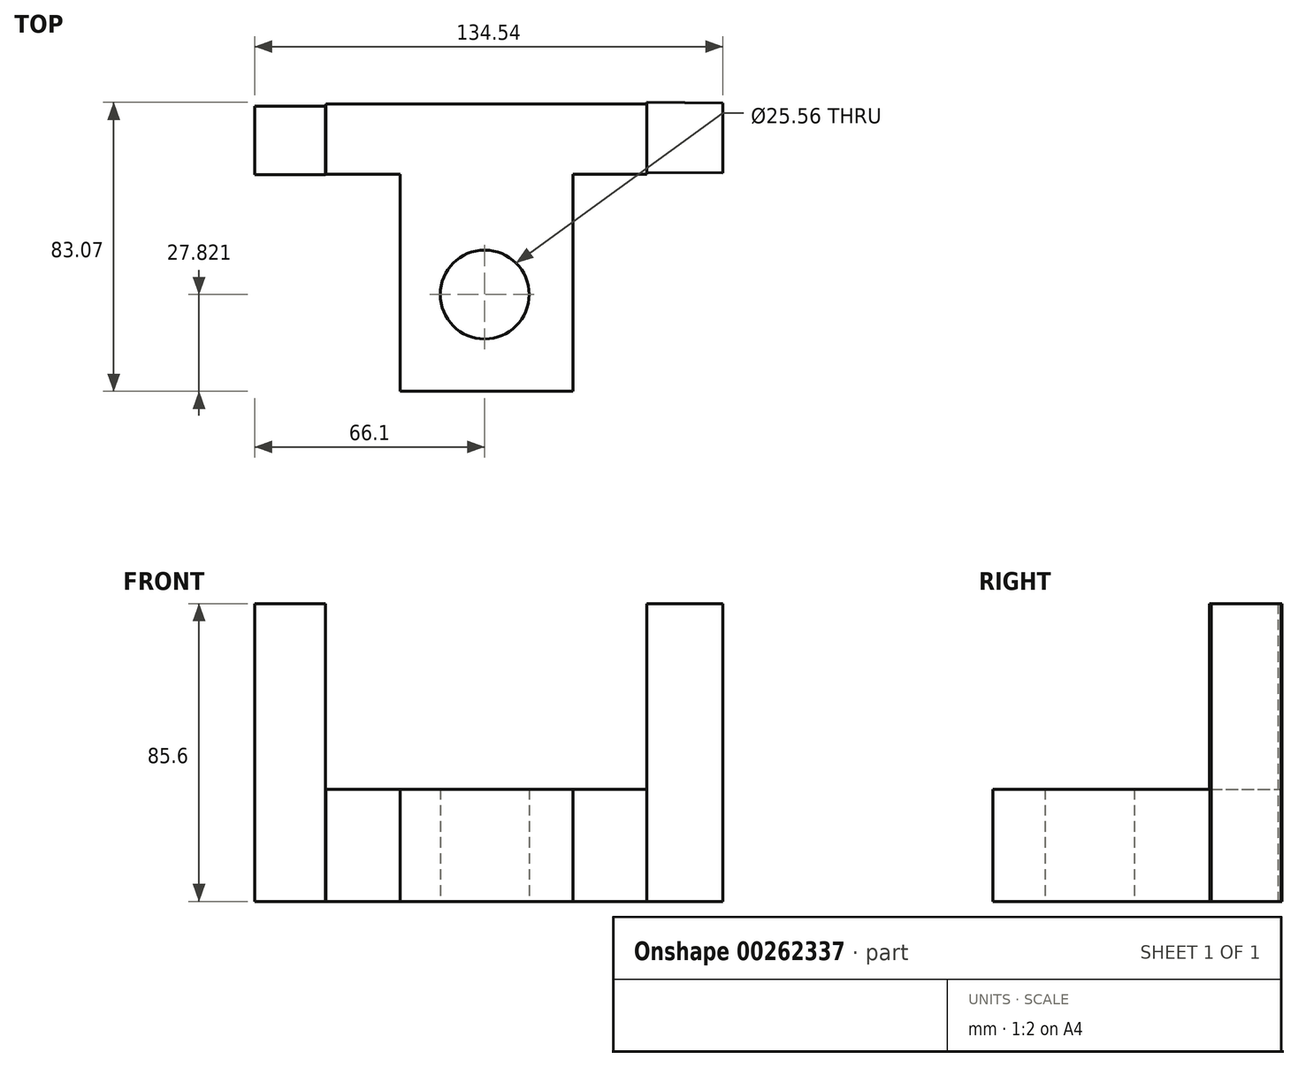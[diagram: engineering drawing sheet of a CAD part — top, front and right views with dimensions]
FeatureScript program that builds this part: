
annotation { "Feature Type Name" : "Feature", "Feature Type Description" : "" }
export const myFeature = defineFeature(function(context is Context, id is Id, definition is map)
    precondition{}
    {
        {
            var Q0;
            Q0=qCreatedBy(makeId("Top.planeOp"),FACE);
            var sketch = newSketch(context, id + "F0", { "sketchPlane" : qUnion([Q0])});
            skLineSegment(sketch, "E0.top", {"start": v(-24.33, -38.9) * mm, "end": v(25.36, -38.9) * mm});
            skLineSegment(sketch, "E0.left", {"start": v(-24.33, 23.47) * mm, "end": v(-24.33, -38.9) * mm});
            skLineSegment(sketch, "E0.right", {"start": v(25.36, 23.47) * mm, "end": v(25.36, -38.9) * mm});
            skLineSegment(sketch, "E1", {"start": v(-24.33, 23.47) * mm, "end": v(-45.57, 23.47) * mm});
            skLineSegment(sketch, "E2", {"start": v(25.36, 23.47) * mm, "end": v(46.6, 23.47) * mm});
            skLineSegment(sketch, "E3", {"start": v(-45.57, 23.47) * mm, "end": v(-45.57, 43.7) * mm});
            skLineSegment(sketch, "E4", {"start": v(-45.57, 43.7) * mm, "end": v(46.6, 43.7) * mm});
            skLineSegment(sketch, "E5", {"start": v(46.6, 43.7) * mm, "end": v(46.6, 23.47) * mm});
            skSolve(sketch);
        }
        {
            var Q0;
            Q0 = qSketchRegion(id + "F0", true);
            extrude(context, id + "F1", {"entities" : qUnion([Q0]), "depth" : 32.26 * mm});
        }
        {
            var Q0;
            Q0=qCreatedBy(makeId("Top.planeOp"),FACE);
            var sketch = newSketch(context, id + "F2", { "sketchPlane" : qUnion([Q0])});
            skLineSegment(sketch, "E6.bottom", {"start": v(-45.81, 43.03) * mm, "end": v(-66.1, 43.03) * mm});
            skLineSegment(sketch, "E6.top", {"start": v(-45.81, 23.4) * mm, "end": v(-66.1, 23.4) * mm});
            skLineSegment(sketch, "E6.left", {"start": v(-45.81, 43.03) * mm, "end": v(-45.81, 23.4) * mm});
            skLineSegment(sketch, "E6.right", {"start": v(-66.1, 43.03) * mm, "end": v(-66.1, 23.4) * mm});
            skLineSegment(sketch, "E7", {"start": v(46.56, 44.18) * mm, "end": v(46.56, 24.02) * mm});
            skLineSegment(sketch, "E8", {"start": v(46.56, 24.02) * mm, "end": v(68.38, 23.84) * mm});
            skLineSegment(sketch, "E9", {"start": v(68.38, 23.84) * mm, "end": v(68.44, 43.97) * mm});
            skLineSegment(sketch, "E10", {"start": v(46.56, 44.18) * mm, "end": v(68.44, 43.97) * mm});
            skSolve(sketch);
        }
        {
            var Q0;
            Q0 = qSketchRegion(id + "F2", true);
            extrude(context, id + "F3", {"entities" : qUnion([Q0]), "operationType" : NewBodyOperationType.ADD, "depth" : 85.6 * mm});
        }
        {
            var Q0;
            Q0=qCreatedBy(makeId("Top.planeOp"),FACE);
            var sketch = newSketch(context, id + "F4", { "sketchPlane" : qUnion([Q0])});
            skCircle(sketch, "E11", {"center": v(0, -11.07) * mm, "radius": 12.78 * mm});
            skSolve(sketch);
        }
        {
            var Q0;
            Q0 = qSketchRegion(id + "F4", true);
            extrude(context, id + "F5", {"entities" : qUnion([Q0]), "operationType" : NewBodyOperationType.REMOVE, "depth" : 52.07 * mm});
        }
    });
